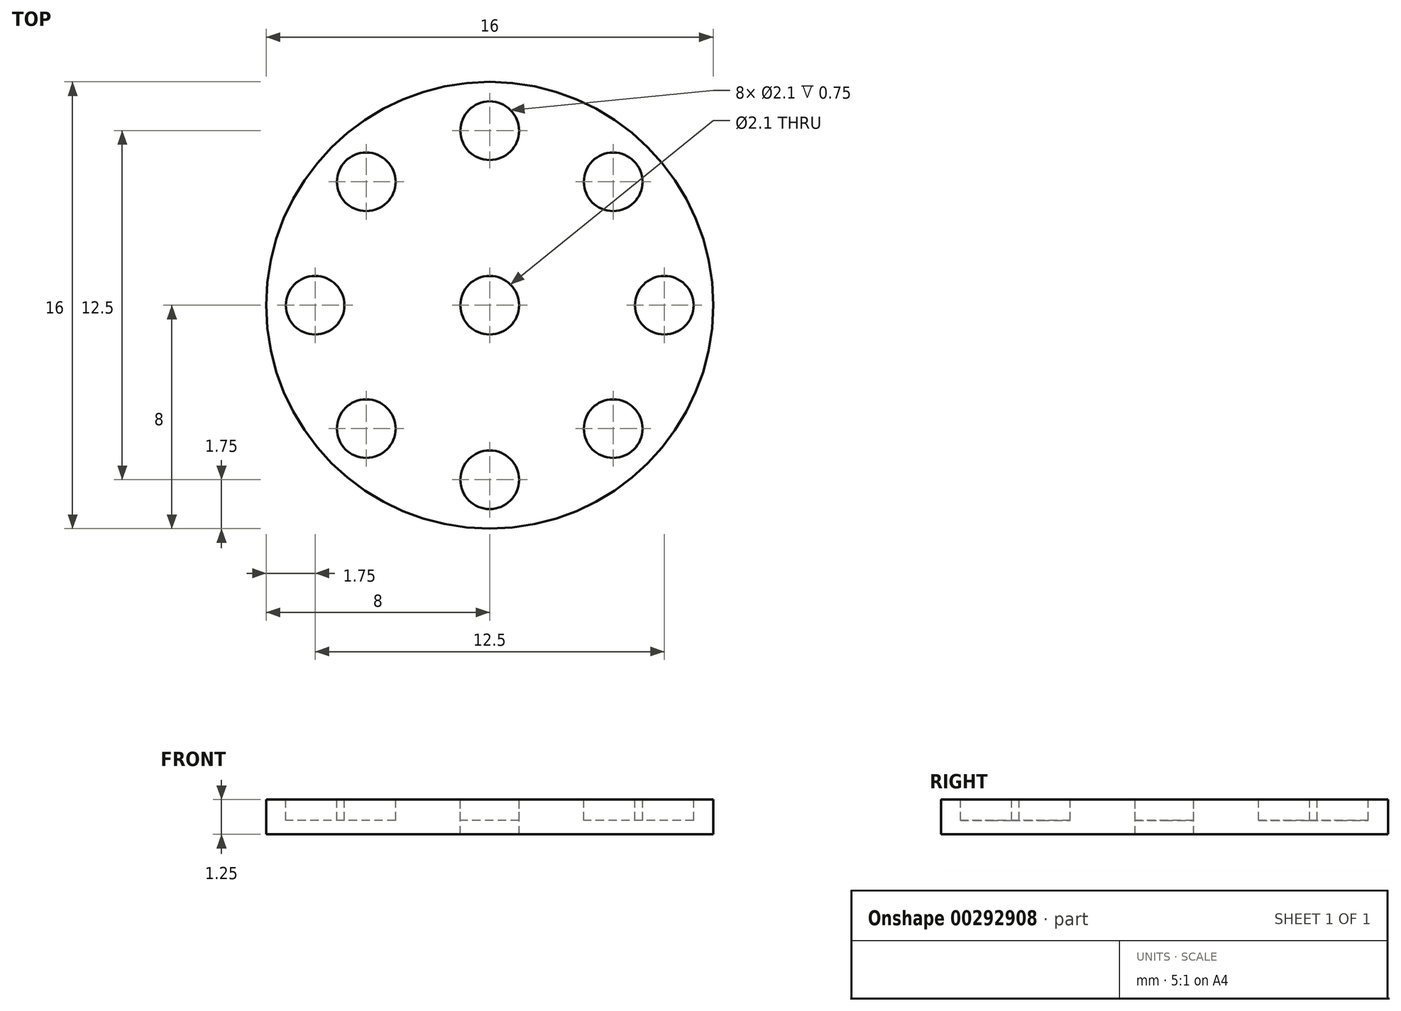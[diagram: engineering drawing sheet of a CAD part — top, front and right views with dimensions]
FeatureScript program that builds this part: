
annotation { "Feature Type Name" : "Feature", "Feature Type Description" : "" }
export const myFeature = defineFeature(function(context is Context, id is Id, definition is map)
    precondition{}
    {
        {
            var Q0;
            Q0=qCreatedBy(makeId("Top.planeOp"),FACE);
            var sketch = newSketch(context, id + "F0", { "sketchPlane" : qUnion([Q0])});
            skCircle(sketch, "E0", {"center": v(0, 0) * mm, "radius": 8 * mm});
            skSolve(sketch);
        }
        {
            var Q0;
            Q0 = qSketchRegion(id + "F0", true);
            extrude(context, id + "F1", {"entities" : qUnion([Q0]), "depth" : 1.25 * mm});
        }
        {
            var Q0;
            Q0=makeQuery(id+"F1.opExtrude","CAP_FACE",FACE,{"disambiguationData":[OSD([sQuery(id+"F0.wireOp",EDGE,"E0")])],"isStart":false});
            var sketch = newSketch(context, id + "F2", { "sketchPlane" : qUnion([Q0])});
            skCircle(sketch, "E1", {"center": v(0, 0) * mm, "radius": 1.05 * mm});
            skSolve(sketch);
        }
        {
            var Q0;
            Q0 = qSketchRegion(id + "F2", true);
            extrude(context, id + "F3", {"entities" : qUnion([Q0]), "operationType" : NewBodyOperationType.REMOVE, "oppositeDirection" : true, "depth" : 25 * mm});
        }
        {
            var Q0;
            Q0=makeQuery(id+"F1.opExtrude","CAP_FACE",FACE,{"disambiguationData":[OSD([sQuery(id+"F0.wireOp",EDGE,"E0")])],"isStart":false});
            var sketch = newSketch(context, id + "F4", { "sketchPlane" : qUnion([Q0])});
            skLineSegment(sketch, "E2", {"start": v(0, 0) * mm, "end": v(0, 6.25) * mm, "construction": true});
            skCircle(sketch, "E3", {"center": v(0, 6.25) * mm, "radius": 1.05 * mm});
            skCircle(sketch, "E4.1.0", {"center": v(-4.42, 4.42) * mm, "radius": 1.05 * mm});
            skCircle(sketch, "E4.2.0", {"center": v(-6.25, 0) * mm, "radius": 1.05 * mm});
            skCircle(sketch, "E4.3.0", {"center": v(-4.42, -4.42) * mm, "radius": 1.05 * mm});
            skCircle(sketch, "E4.4.0", {"center": v(0, -6.25) * mm, "radius": 1.05 * mm});
            skCircle(sketch, "E4.5.0", {"center": v(4.42, -4.42) * mm, "radius": 1.05 * mm});
            skCircle(sketch, "E4.6.0", {"center": v(6.25, 0) * mm, "radius": 1.05 * mm});
            skCircle(sketch, "E4.7.0", {"center": v(4.42, 4.42) * mm, "radius": 1.05 * mm});
            skPoint(sketch, "E4.center", {"position": v(0, 0) * mm});
            skSolve(sketch);
        }
        {
            var Q0;
            Q0 = qSketchRegion(id + "F4", true);
            extrude(context, id + "F5", {"entities" : qUnion([Q0]), "operationType" : NewBodyOperationType.REMOVE, "oppositeDirection" : true, "depth" : 0.75 * mm});
        }
    });
